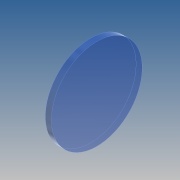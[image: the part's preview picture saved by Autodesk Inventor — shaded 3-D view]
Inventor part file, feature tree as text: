
AUTODESK INVENTOR PART (.ipt)
format: ipt  version: 2017 (Build 210142000, 142)  size: 187,904 bytes
history: native  units: mm
features: revolve x1, sketch x1
ambient origin geometry x8: Origin, YZ Plane, XZ Plane, XY Plane, X Axis, Y Axis, Z Axis, Center Point
bodies: Solid1 (feature_tree)
feature tree (2):
  revolve  "Revolution1"  [1 undecoded]
  sketch  "Sketch1"  dims[d0=30.0mm d1=2.0mm d2=4.5mm d3=90.0deg]
note: 1 required parameter value undecoded (feature->parameter linkage not recoverable at this tier; creation-order binding heuristic only, values carry confidence <= 0.55)
